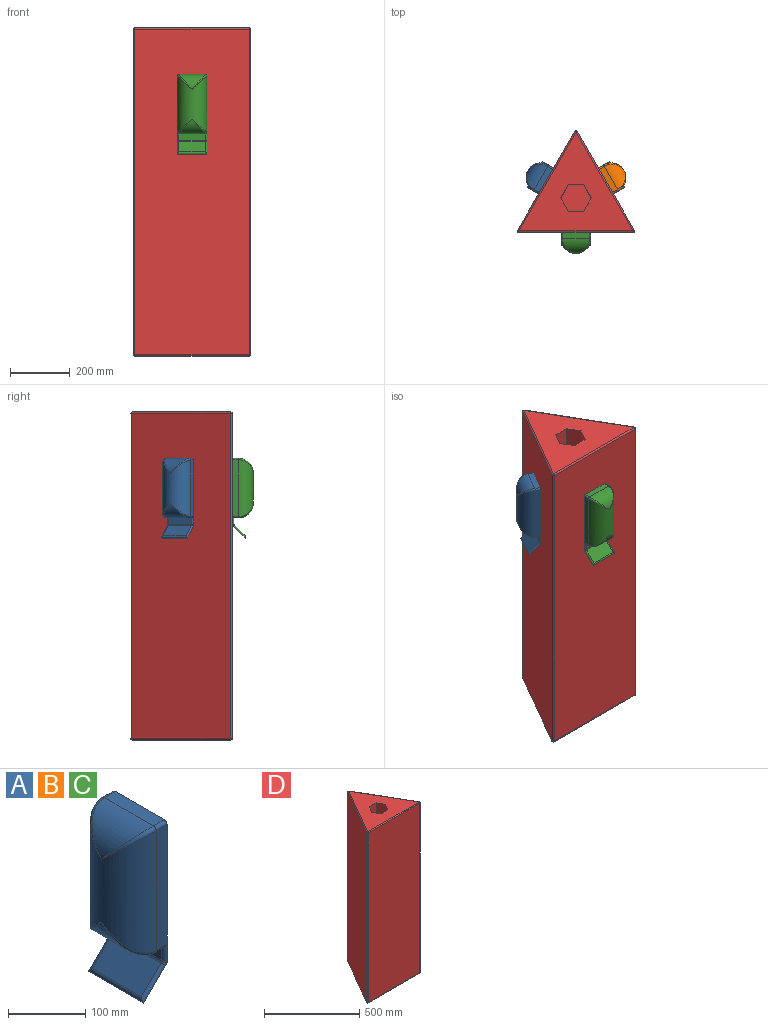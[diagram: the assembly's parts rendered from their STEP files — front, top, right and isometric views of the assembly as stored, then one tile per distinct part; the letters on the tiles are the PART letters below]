
ASSEMBLY  parts=4 mates=3
PART A: 29 faces, bbox 74.7x100x267.4 mm
  f0: plane 7.07x2.93mm, normal (0,1,0), area 2.2mm2, adj f3,f5,f9
  f1: plane 7.07x2.93mm, normal (0,-1,0), area 2.2mm2, adj f3,f5,f12
  f2: plane 90x20.86mm, normal (-1,0,0), area 1877.2mm2, adj f7,f11,f13,f15
  f3: plane 225x100mm, normal (1,0,0), area 22489.3mm2, adj f0,f1,f5,f7,f13,f14,f16,f17
  f4: plane 90x35.96mm, normal (-0.71,0,0.71), area 4577.2mm2, adj f6,f8,f10,f11
  f5: plane 100x42.43mm, normal (0.71,0,-0.71), area 6000mm2, adj f0,f1,f3,f6,f8,f10
  f6: cylinder r=5mm len=43.03mm, axis (-0.71,0,-0.71), area 424.4mm2, adj f4,f5,f8,f9
  f7: cylinder r=5mm len=25.86mm, axis (0,0,-1), area 178.1mm2, adj f2,f3,f9,f21
  f8: cylinder r=5mm len=100mm, axis (0,-1,0), area 756.9mm2, adj f4,f5,f6,f10
  f9: torus R=10mm, axis (0,1,0), area 42.1mm2, adj f0,f6,f7,f11
  f10: cylinder r=5mm len=43.03mm, axis (0.71,0,0.71), area 424.4mm2, adj f4,f5,f8,f12
  f11: cylinder r=5mm len=90mm, axis (0,-1,0), area 353.4mm2, adj f2,f4,f9,f12
  f12: torus R=10mm, axis (0,1,0), area 42.1mm2, adj f1,f10,f11,f13
  f13: cylinder r=5mm len=25.86mm, axis (0,0,1), area 178.1mm2, adj f2,f3,f12,f24
  f14: plane 190x20mm, normal (0,1,0), area 3800mm2, adj f3,f19,f21,f25
  f15: plane 90x15mm, normal (0,0,-1), area 1350mm2, adj f2,f20,f21,f24
  f16: plane 190x20mm, normal (0,-1,0), area 3800mm2, adj f3,f19,f24,f28
  f17: plane 90x20mm, normal (0,0,1), area 1800mm2, adj f3,f18,f25,f28
  f18: cylinder r=50mm len=90mm, axis (0,1,0), area 4500mm2, adj f17,f26,f27
  f19: cylinder r=50mm len=190mm, axis (0,0,-1), area 24708mm2, adj f14,f16,f22,f23,f26,f27
  f20: cylinder r=50mm len=90mm, axis (0,-1,0), area 4500mm2, adj f15,f22,f23
  f21: cylinder r=5mm len=20mm, axis (1,0,0), area 132.1mm2, adj f7,f14,f15,f22
  f22: bspline ~51.8x50mm, area 428.4mm2, adj f19,f20,f21
  f23: bspline ~57.16x50mm, area 428.4mm2, adj f19,f20,f24
  f24: cylinder r=5mm len=20mm, axis (1,0,0), area 132.1mm2, adj f13,f15,f16,f23
  f25: cylinder r=5mm len=20mm, axis (-1,0,0), area 157.1mm2, adj f3,f14,f17,f26
  f26: bspline ~51.8x50mm, area 428.4mm2, adj f18,f19,f25
  f27: bspline ~57.16x50mm, area 428.4mm2, adj f18,f19,f28
  f28: cylinder r=5mm len=20mm, axis (-1,0,0), area 157.1mm2, adj f3,f16,f17,f27
PART B: same geometry as A
PART C: same geometry as A
PART D: 27 faces, bbox 392.7x341.4x1100 mm
  f0: plane 1090x331.41mm, normal (-0.87,0.5,0), area 417120.6mm2, adj f6,f14,f15,f19
  f1: plane 1090x382.68mm, normal (0,-1,0), area 417120.6mm2, adj f8,f13,f16,f19
  f2: plane 1090x331.41mm, normal (0.87,0.5,0), area 417120.6mm2, adj f5,f6,f7,f8
  f3: plane 382.68x331.41mm, normal (0,0,-1), area 63411.9mm2, adj f5,f13,f14
  f4: plane 382.68x331.41mm, normal (0,0,1), area 56654.3mm2, adj f7,f15,f16,f20,f21,f22,f23,f24
  f5: cylinder r=5mm len=333.91mm, axis (0.5,-0.87,0), area 3005.6mm2, adj f2,f3,f9,f10
  f6: cylinder r=5mm len=1090mm, axis (0,0,-1), area 11414.5mm2, adj f0,f2,f10,f11
  f7: cylinder r=5mm len=333.91mm, axis (-0.5,0.87,0), area 3005.6mm2, adj f2,f4,f11,f12
  f8: cylinder r=5mm len=1090mm, axis (0,0,1), area 11414.5mm2, adj f1,f2,f9,f12
  f9: sphere r=5mm, area 52.4mm2, adj f5,f8,f13
  f10: sphere r=5mm, area 52.4mm2, adj f5,f6,f14
  f11: sphere r=5mm, area 52.4mm2, adj f6,f7,f15
  f12: sphere r=5mm, area 52.4mm2, adj f7,f8,f16
  f13: cylinder r=5mm len=382.68mm, axis (-1,0,0), area 3005.6mm2, adj f1,f3,f9,f17
  f14: cylinder r=5mm len=333.91mm, axis (0.5,0.87,0), area 3005.6mm2, adj f0,f3,f10,f17
  f15: cylinder r=5mm len=333.91mm, axis (-0.5,-0.87,0), area 3005.6mm2, adj f0,f4,f11,f18
  f16: cylinder r=5mm len=382.68mm, axis (1,0,0), area 3005.6mm2, adj f1,f4,f12,f18
  f17: sphere r=5mm, area 52.4mm2, adj f13,f14,f19
  f18: sphere r=5mm, area 52.4mm2, adj f15,f16,f19
  f19: cylinder r=5mm len=1090mm, axis (0,0,-1), area 11414.5mm2, adj f0,f1,f17,f18
  f20: plane 300x44.17mm, normal (-0.87,-0.5,0), area 15300mm2, adj f4,f21,f25,f26
  f21: plane 300x51mm, normal (0,-1,0), area 15300mm2, adj f4,f20,f22,f26
  f22: plane 300x44.17mm, normal (0.87,-0.5,0), area 15300mm2, adj f4,f21,f23,f26
  f23: plane 300x44.17mm, normal (0.87,0.5,0), area 15300mm2, adj f4,f22,f24,f26
  f24: plane 300x51mm, normal (0,1,0), area 15300mm2, adj f4,f23,f25,f26
  f25: plane 300x44.17mm, normal (-0.87,0.5,0), area 15300mm2, adj f4,f20,f24,f26
  f26: plane 102x88.33mm, normal (0,0,1), area 6757.6mm2, adj f20,f21,f22,f23,f24,f25
PLACE A rot(axis=(0,0,-1),30deg) t=(-80.5,206.98,-5.89)mm
PLACE B rot(axis=(0,0,-1),150deg) t=(119.5,120.38,-5.39)mm
PLACE C rot(axis=(0,0,1),90deg) t=(-55.5,-9.53,-5.89)mm
PLACE D t=(-5.5,-9.53,249.56)mm
MATE parallel A.f3 <-> D.f0  axis (0.87,-0.5,0) through (-105.5,163.68,-18.44)mm
MATE parallel C.f3 <-> D.f1  axis (0,1,0) through (-5.5,-9.53,-18.44)mm
MATE parallel B.f3 <-> D.f2  axis (-0.87,-0.5,0) through (94.5,163.68,-17.94)mm
